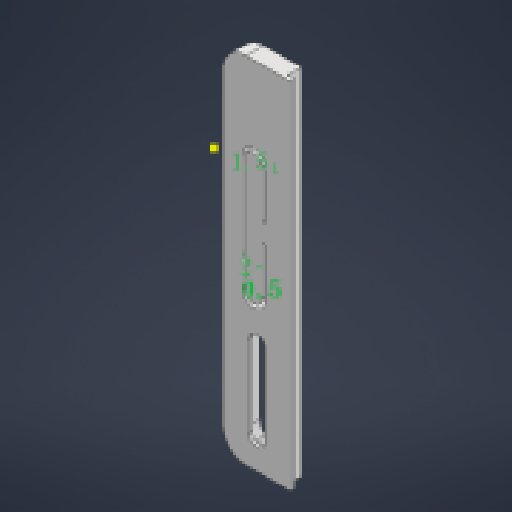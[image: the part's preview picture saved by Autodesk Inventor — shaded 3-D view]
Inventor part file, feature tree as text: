
AUTODESK INVENTOR PART (.ipt)
format: ipt  version: 2025 (Build 290162000, 162)  size: 434,688 bytes
history: native  units: mm
features: reference x15, extrude x14, sketch x13, other x12, projected_geometry x6, fillet x3, plane x1
ambient origin geometry x8: Origin, YZ Plane, XZ Plane, XY Plane, X Axis, Y Axis, Z Axis, Center Point
bodies: 实体1 (feature_tree)
feature tree (64):
  extrude  "拉伸1"  Depth=10.0mm TaperAngle=0.0deg
  sketch  "草图2"  dims[d4=10.0mm d5=0.0mm d6=0.2mm]
  plane  "工作平面1"
  extrude  "拉伸2"  Depth=10.0mm
  extrude  "拉伸3"  Depth=0.4mm TaperAngle=0.0deg
  extrude  "拉伸4"  Depth=3.4mm
  sketch  "草图5"  dims[d14=1.0mm d15=3.9mm d16=0.0mm]
  extrude  "拉伸5"  Depth=1.0mm TaperAngle=0.0deg
  extrude  "拉伸6"  Depth=4.5mm
  extrude  "拉伸7"  Depth=1.5mm TaperAngle=0.0deg
  fillet  "圆角1"  Radius=0.2mm
  fillet  "圆角2"  Radius=1.0mm
  extrude  "拉伸8"  Depth=1.5mm TaperAngle=0.0deg
  fillet  "圆角3"  Radius=0.2mm
  extrude  "拉伸10"  Depth=1.1mm TaperAngle=0.0deg
  other  "直接编辑1"
  extrude  "拉伸11"  Depth=1.5mm
  extrude  "拉伸12"  Depth=4.0mm TaperAngle=0.0deg
  extrude  "拉伸13"  Depth=2.0mm
  extrude  "拉伸14"  Depth=1.5mm TaperAngle=0.0deg
  other  "直接编辑3"
  extrude  "拉伸15"  Depth=1.5mm TaperAngle=0.0deg
  sketch  "草图1"  dims[d0=3.0mm d1=0.0mm d2=10.0mm d3=0.0mm]
  reference  "参考1"
  reference  "参考2"
  reference  "参考3"
  reference  "参考4"
  reference  "参考5"
  reference  "参考6"
  sketch  "草图3"  dims[d7=0.2mm d8=0.4mm d9=0.0mm]
  reference  "参考8"
  reference  "参考9"
  sketch  "草图4"  dims[d11=20.4mm d13=3.4mm]
  projected_geometry  "投影回路1"
  sketch  "草图8"  dims[d18=0.5mm d19=0.0mm d20=4.5mm]
  reference  "参考11"
  reference  "参考12"
  projected_geometry  "投影回路2"
  sketch  "草图11"  dims[d21=4.5mm d22=1.5mm d23=0.0mm d24=0.2mm d25=1.0mm]
  sketch  "草图12"  dims[d26=1.5mm d27=1.1mm d28=0.0mm d29=0.2mm]
  reference  "参考13"
  reference  "参考14"
  sketch  "草图13"  dims[d33=2.0mm d35=1.1mm d36=0.0mm]
  projected_geometry  "投影回路3"
  projected_geometry  "投影回路4"
  projected_geometry  "投影回路5"
  sketch  "草图14"  dims[d37=0.0mm d38=0.0mm d39=-0.5mm d41=1.5mm]
  projected_geometry  "投影回路6"
  sketch  "草图15"  dims[d42=0.5mm d43=4.0mm d44=0.0mm]
  sketch  "草图16"  dims[d45=15.0mm d46=0.0mm d47=2.0mm]
  sketch  "草图17"  dims[d48=6.0mm d49=0.0mm d50=4.0mm d51=0.0mm d52=1.5mm d53=0.0mm]
  reference  "参考15"
  reference  "参考16"
  reference  "参考17"
  parser-record x2  (decoder bookkeeping rows leaked as tree rows — omitted from the tree; the rows remain in map.json)
  other  "装配体.iam"
  other  "键盘外壳:1"
  other  "dlc.iam"
  other  "指纹识别:1"
  other  "音量接口:1"
  other  "移动1"
  other  "删除2"
  other  "指纹安装板:1"
note: 2 file-system paths scrubbed to <path> (originals preserved in map.json)
